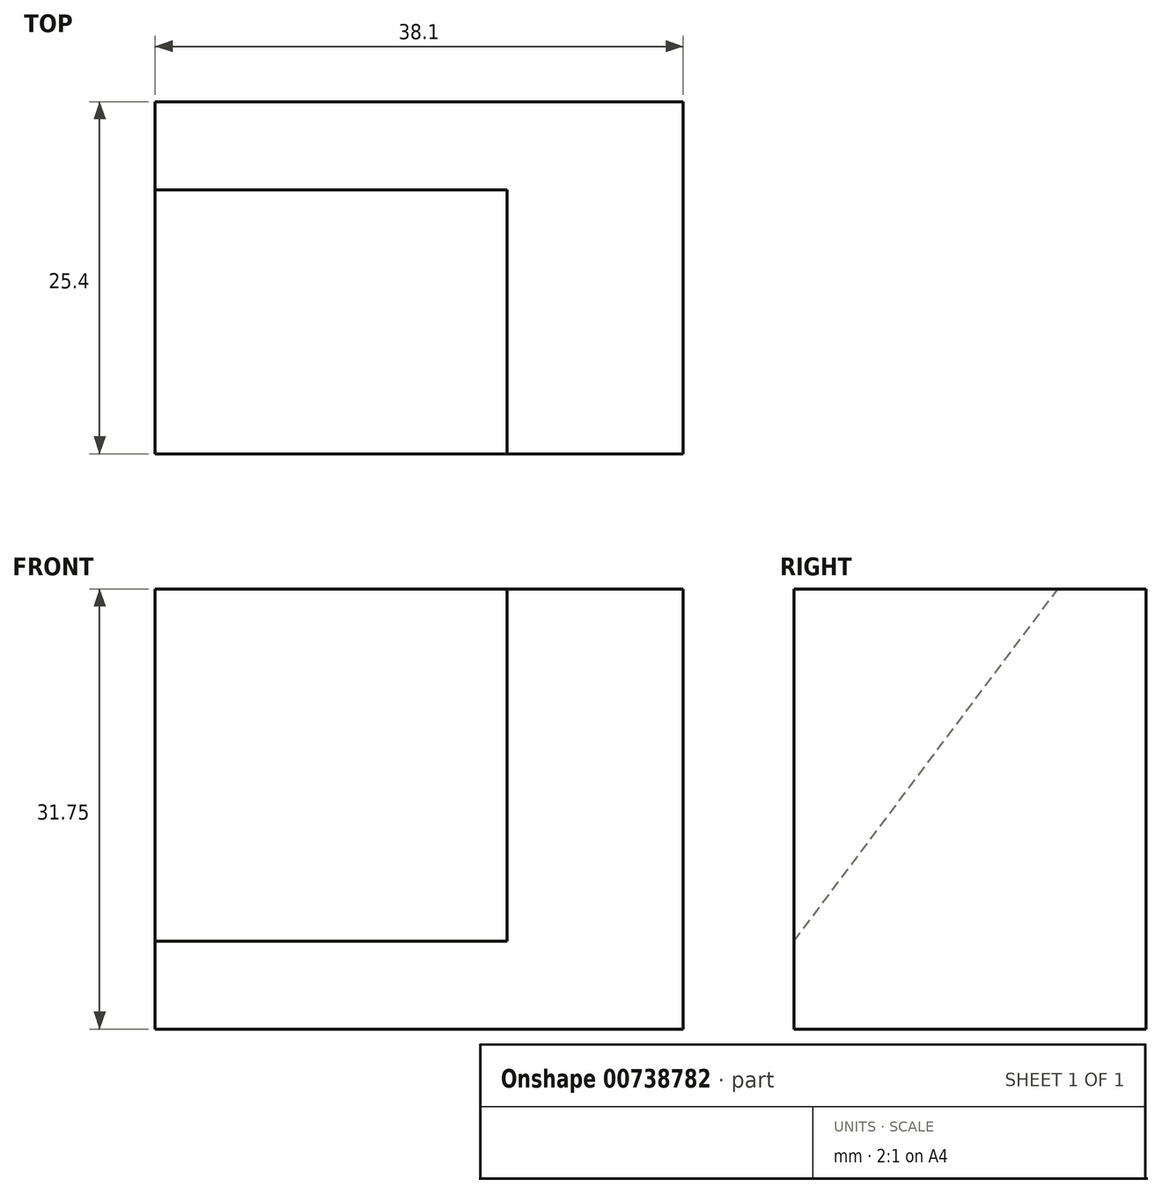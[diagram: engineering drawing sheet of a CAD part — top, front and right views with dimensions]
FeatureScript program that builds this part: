
annotation { "Feature Type Name" : "Feature", "Feature Type Description" : "" }
export const myFeature = defineFeature(function(context is Context, id is Id, definition is map)
    precondition{}
    {
        {
            var Q0;
            Q0=qCreatedBy(makeId("Right.planeOp"),FACE);
            var sketch = newSketch(context, id + "F0", { "sketchPlane" : qUnion([Q0])});
            skLineSegment(sketch, "E0", {"start": v(0, 0) * mm, "end": v(0, 31.75) * mm});
            skLineSegment(sketch, "E1", {"start": v(0, 31.75) * mm, "end": v(25.4, 31.75) * mm});
            skLineSegment(sketch, "E2", {"start": v(25.4, 31.75) * mm, "end": v(25.4, 0) * mm});
            skLineSegment(sketch, "E3", {"start": v(25.4, 0) * mm, "end": v(0, 0) * mm});
            skSolve(sketch);
        }
        {
            var Q0;
            Q0 = qSketchRegion(id + "F0", true);
            extrude(context, id + "F1", {"entities" : qUnion([Q0]), "depth" : 38.1 * mm, "offsetDistance" : 25.4 * mm});
        }
        {
            var Q0;
            Q0=qCreatedBy(makeId("Right.planeOp"),FACE);
            var sketch = newSketch(context, id + "F2", { "sketchPlane" : qUnion([Q0])});
            skLineSegment(sketch, "E4", {"start": v(0, 6.35) * mm, "end": v(19.05, 31.75) * mm});
            skLineSegment(sketch, "E5", {"start": v(19.05, 31.75) * mm, "end": v(0, 31.75) * mm});
            skLineSegment(sketch, "E6", {"start": v(0, 31.75) * mm, "end": v(0, 6.35) * mm});
            skSolve(sketch);
        }
        {
            var Q0;
            Q0 = qSketchRegion(id + "F2", true);
            extrude(context, id + "F3", {"entities" : qUnion([Q0]), "operationType" : NewBodyOperationType.REMOVE, "depth" : 25.4 * mm, "offsetDistance" : 25.4 * mm});
        }
    });
